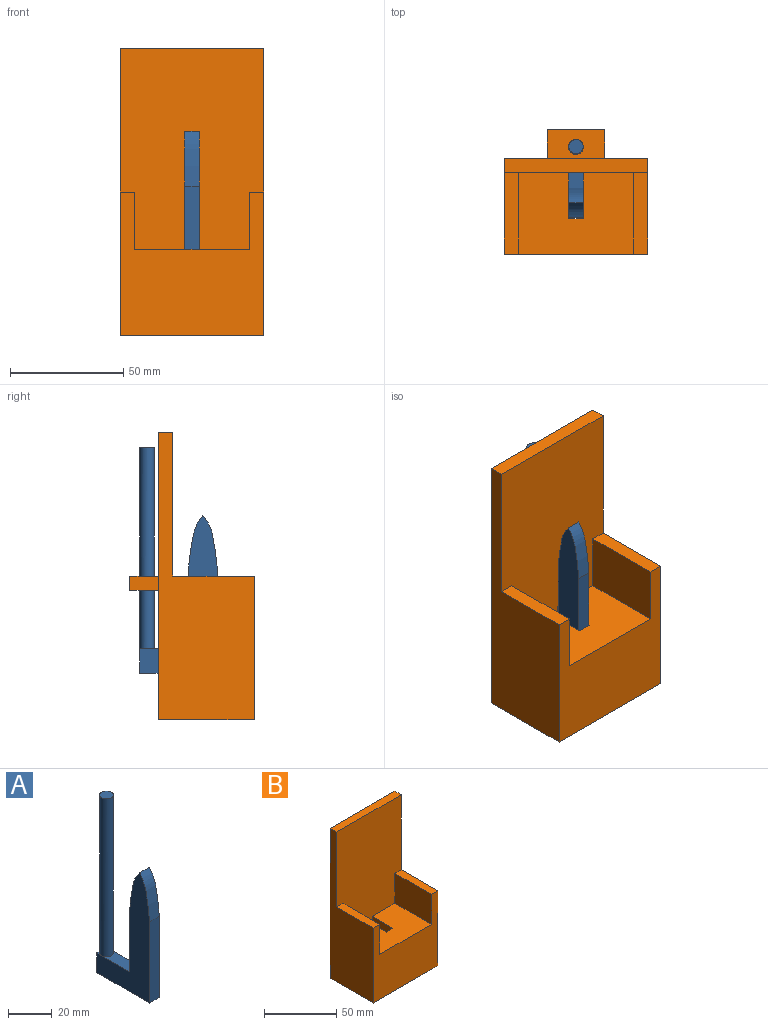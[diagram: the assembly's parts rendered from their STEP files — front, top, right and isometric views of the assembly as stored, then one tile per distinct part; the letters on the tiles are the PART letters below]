
ASSEMBLY  parts=2 mates=2
PART A: 13 faces, bbox 6.4x34.4x99.9 mm
  f0: plane 3.18x3.18mm, normal (0,0,1), area 2.2mm2, adj f2,f9,f11
  f1: plane 3.18x3.18mm, normal (0,0,1), area 2.2mm2, adj f2,f10,f11
  f2: plane 11.02x6.35mm, normal (0,1,0), area 70mm2, adj f0,f1,f8,f9,f10
  f3: plane 18.23x6.35mm, normal (0,0,1), area 99.9mm2, adj f4,f9,f10,f11
  f4: plane 34.65x6.35mm, normal (0,1,0), area 220mm2, adj f3,f5,f9,f10
  f5: extruded ~24.36x6.49mm, area 162.6mm2, adj f4,f6,f9,f10
  f6: extruded ~24.36x6.49mm, area 162.6mm2, adj f5,f7,f9,f10
  f7: plane 45.68x6.35mm, normal (0,-1,0), area 290mm2, adj f6,f8,f9,f10
  f8: plane 34.37x6.35mm, normal (0,0,-1), area 218.3mm2, adj f2,f7,f9,f10
  f9: plane 70.04x34.37mm, normal (1,0,0), area 1046.3mm2, adj f0,f2,f3,f4,f5,f6,f7,f8
  f10: plane 70.04x34.37mm, normal (-1,0,0), area 1046.3mm2, adj f1,f2,f3,f4,f5,f6,f7,f8
  f11: cylinder r=3.17mm len=88.9mm, axis (0,0,-1), area 1773.5mm2, adj f0,f1,f3,f12
  f12: plane 6.35x6.35mm, normal (0,0,1), area 31.7mm2, adj f11
PART B: 25 faces, bbox 63.5x55x127 mm
  f0: plane 50.8x35.98mm, normal (0,0,1), area 1698.9mm2, adj f7,f10,f11,f12,f16,f17,f18
  f1: plane 50.8x35.98mm, normal (0,0,-1), area 1698.9mm2, adj f6,f10,f13,f14,f15,f16,f17,f18
  f2: plane 63.5x42.33mm, normal (0,0,-1), area 860.2mm2, adj f5,f6,f7,f8,f13,f14,f15
  f3: plane 35.98x6.35mm, normal (0,0,1), area 228.5mm2, adj f7,f8,f10,f11
  f4: plane 63.5x6.35mm, normal (0,0,1), area 403.2mm2, adj f5,f6,f8,f10
  f5: plane 127x42.33mm, normal (1,0,0), area 3091.4mm2, adj f2,f4,f6,f7,f9,f10
  f6: plane 127x63.5mm, normal (0,1,0), area 6290.3mm2, adj f1,f2,f4,f5,f8,f13,f14,f19
  f7: plane 63.5x63.5mm, normal (0,-1,0), area 2741.9mm2, adj f0,f2,f3,f5,f8,f9,f11,f12
  f8: plane 127x42.33mm, normal (-1,0,0), area 3091.4mm2, adj f2,f3,f4,f6,f7,f10
  f9: plane 35.98x6.35mm, normal (0,0,1), area 228.5mm2, adj f5,f7,f10,f12
  f10: plane 95.25x63.5mm, normal (0,-1,0), area 5362.9mm2, adj f0,f1,f3,f4,f5,f8,f9,f11
  f11: plane 35.98x25.4mm, normal (1,0,0), area 914mm2, adj f0,f3,f7,f10
  f12: plane 35.98x25.4mm, normal (-1,0,0), area 914mm2, adj f0,f7,f9,f10
  f13: plane 35.98x31.75mm, normal (1,0,0), area 1142.5mm2, adj f1,f2,f6,f15
  f14: plane 35.98x31.75mm, normal (-1,0,0), area 1142.5mm2, adj f1,f2,f6,f15
  f15: plane 50.8x31.75mm, normal (0,1,0), area 1612.9mm2, adj f1,f2,f13,f14
  f16: plane 20.32x6.35mm, normal (1,0,0), area 129mm2, adj f0,f1,f10,f17
  f17: plane 6.35x6.35mm, normal (0,1,0), area 40.3mm2, adj f0,f1,f16,f18
  f18: plane 20.32x6.35mm, normal (-1,0,0), area 129mm2, adj f0,f1,f10,f17
  f19: plane 12.7x6.35mm, normal (1,0,0), area 80.6mm2, adj f6,f20,f22,f23
  f20: plane 25.4x12.7mm, normal (0,0,-1), area 288.3mm2, adj f6,f19,f21,f23,f24
  f21: plane 12.7x6.35mm, normal (-1,0,0), area 80.6mm2, adj f6,f20,f22,f23
  f22: plane 25.4x12.7mm, normal (0,0,1), area 288.3mm2, adj f6,f19,f21,f23,f24
  f23: plane 25.4x6.35mm, normal (0,1,0), area 161.3mm2, adj f19,f20,f21,f22
  f24: cylinder r=3.3mm len=6.6mm, axis (0,0,1), area 131.7mm2, adj f20,f22
PLACE A t=(-11.92,-41.23,-49.58)mm
PLACE B t=(-40.49,14.72,-25.93)mm fixed
MATE slider A.f11 <-> B.f24  axis (0,0,-1) through (-8.74,19.8,49.94)mm
MATE parallel A.f9 <-> B.f5  axis (1,0,0) through (-5.57,-1.03,20.17)mm
